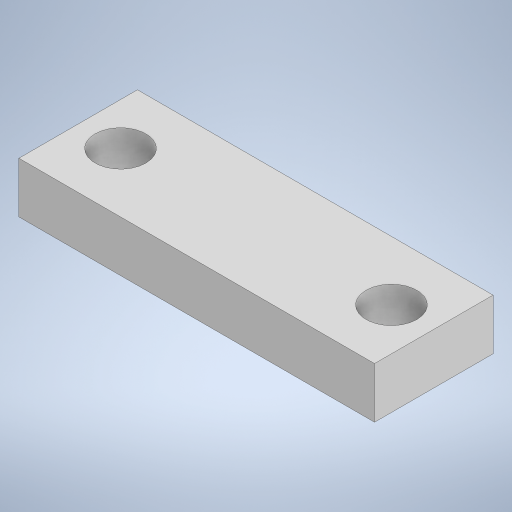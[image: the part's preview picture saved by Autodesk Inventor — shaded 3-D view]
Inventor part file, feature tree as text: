
AUTODESK INVENTOR PART (.ipt)
format: ipt  version: 2023.2 (Build 272271000, 271)  size: 524,288 bytes
history: native  units: mm
features: sketch x1, extrude x1, hole x1
ambient origin geometry x8: Origin, YZ Plane, XZ Plane, XY Plane, X Axis, Y Axis, Z Axis, Center Point
bodies: Solid1 (feature_tree)
feature tree (3):
  sketch  "Sketch1"  dims[d0=42.0mm d1=14.0mm d2=5.0mm d3=5.0mm d4=6.0mm d5=0.0mm d6=6.0mm d7=6.0mm d8=4.0mm d9=2.0mm d10=90.0deg d11=8.0mm d12=20.594885mm]
  extrude  "Extrusion1"  Depth=14.0mm
  hole  "Hole1"  [1 undecoded]
note: 1 required parameter value undecoded (feature->parameter linkage not recoverable at this tier; creation-order binding heuristic only, values carry confidence <= 0.55)
